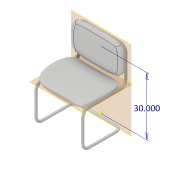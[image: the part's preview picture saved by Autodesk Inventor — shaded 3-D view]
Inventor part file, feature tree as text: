
AUTODESK INVENTOR PART (.ipt)
format: ipt  version: 2017 (Build 210142000, 142)  size: 663,040 bytes
history: native  units: in
note: dims shown in document units (in); Inventor stores cm internally (conversion verified against a paired STEP export)
features: sketch x5, plane x3, other x2, sweep x1, extrude x1, pattern_linear x1
ambient origin geometry x8: Origin, YZ Plane, XZ Plane, XY Plane, X Axis, Y Axis, Z Axis, Center Point
bodies: Solid1 (feature_tree), Solid2 (feature_tree), Solid3 (feature_tree)
feature tree (13):
  sketch  "3D Sketch1"
  plane  "Work Plane1"
  sweep  "Sweep1"
  extrude  "Extrusion1"  Depth=3.0in
  pattern_linear  "Rectangular Pattern1"  Spacing1=3.0in  [1 undecoded]
  plane  "Work Plane2"
  sketch  "Sketch4"  dims[d4=3.0in]
  other  "Form1"
  plane  "Work Plane3"
  sketch  "Sketch5"  dims[d5=3.0in d6=3.0in d7=3.0in d8=3.0in d9=3.0in d10=20.0in d12=12.0in d13=18.0in d14=18.0in d15=22.0in d16=12.0in d17=1.0in d18=1.25in d19=36.0in d20=2.0in d21=0.0in d22=0.0in d23=1.0in d24=1.25in d25=18.0in d26=16.0in d27=1.0in d28=0.0in d29=1.1811in d31=23.0in d32=10.0in d34=30.0in]
  other  "Form2"
  sketch  "Sketch2"  dims[d0=3.0in d1=3.0in]
  sketch  "Sketch3"  dims[d2=3.0in d3=3.0in]
note: 1 required parameter value undecoded (feature->parameter linkage not recoverable at this tier; creation-order binding heuristic only, values carry confidence <= 0.55)
